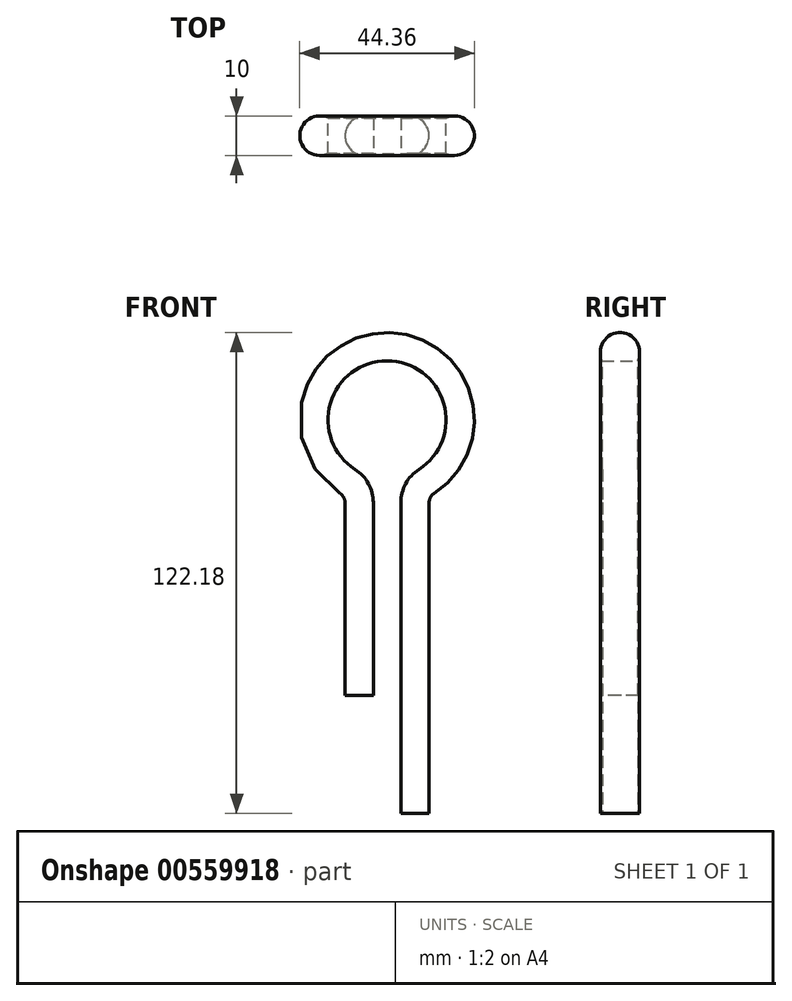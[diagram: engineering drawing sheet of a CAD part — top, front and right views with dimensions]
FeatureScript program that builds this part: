
annotation { "Feature Type Name" : "Feature", "Feature Type Description" : "" }
export const myFeature = defineFeature(function(context is Context, id is Id, definition is map)
    precondition{}
    {
        {
            var Q0;
            Q0=qCreatedBy(makeId("Top.planeOp"),FACE);
            var sketch = newSketch(context, id + "F0", { "sketchPlane" : qUnion([Q0])});
            skArc(sketch, "E0", {"start": v(2.18, 4.5) * mm, "mid": v(-5, 0) * mm, "end": v(2.18, -4.5) * mm});
            skLineSegment(sketch, "E1", {"start": v(2.18, 4.5) * mm, "end": v(2.18, -4.5) * mm});
            skSolve(sketch);
        }
        {
            var Q0;
            Q0=qCreatedBy(makeId("Front.planeOp"),FACE);
            var sketch = newSketch(context, id + "F1", { "sketchPlane" : qUnion([Q0])});
            skLineSegment(sketch, "E2", {"start": v(2.18, 0) * mm, "end": v(2.18, 48.96) * mm});
            skArc(sketch, "E3", {"start": v(13.78, 57.38) * mm, "mid": v(5.68, 85) * mm, "end": v(-2.42, 57.38) * mm});
            skLineSegment(sketch, "E4", {"start": v(9.18, 48.96) * mm, "end": v(9.18, -30) * mm});
            skPoint(sketch, "E5.visualSharp", {"position": v(2.18, 55.41) * mm});
            skArc(sketch, "E5.filletArc", {"start": v(2.18, 48.96) * mm, "mid": v(0.95, 53.75) * mm, "end": v(-2.42, 57.38) * mm});
            skPoint(sketch, "E6.visualSharp", {"position": v(9.18, 55.41) * mm});
            skArc(sketch, "E6.filletArc", {"start": v(13.78, 57.38) * mm, "mid": v(10.4, 53.75) * mm, "end": v(9.18, 48.96) * mm});
            skSolve(sketch);
        }
        {
            var Q0;
            Q0=makeQuery(id+"F0.imprint","IMPRINT",FACE,{"disambiguationData":[TD([[makeQuery(id+"F0.imprint","IMPRINT",EDGE,{"derivedFrom":sQuery(id+"F0.wireOp",EDGE,"E0")}),1.0]])]});
            var Q1;
            Q1=sQuery(id+"F1.wireOp",EDGE,"E2");
            var Q2;
            Q2=sQuery(id+"F1.wireOp",EDGE,"E3");
            var Q3;
            Q3=sQuery(id+"F1.wireOp",EDGE,"E4");
            var Q4;
            Q4=sQuery(id+"F1.wireOp",EDGE,"E5.filletArc");
            var Q5;
            Q5=sQuery(id+"F1.wireOp",EDGE,"E6.filletArc");
            sweep(context, id + "F2", {"profiles" : qUnion([Q0]), "path" : qUnion([Q1, Q2, Q3, Q4, Q5])});
        }
    });
